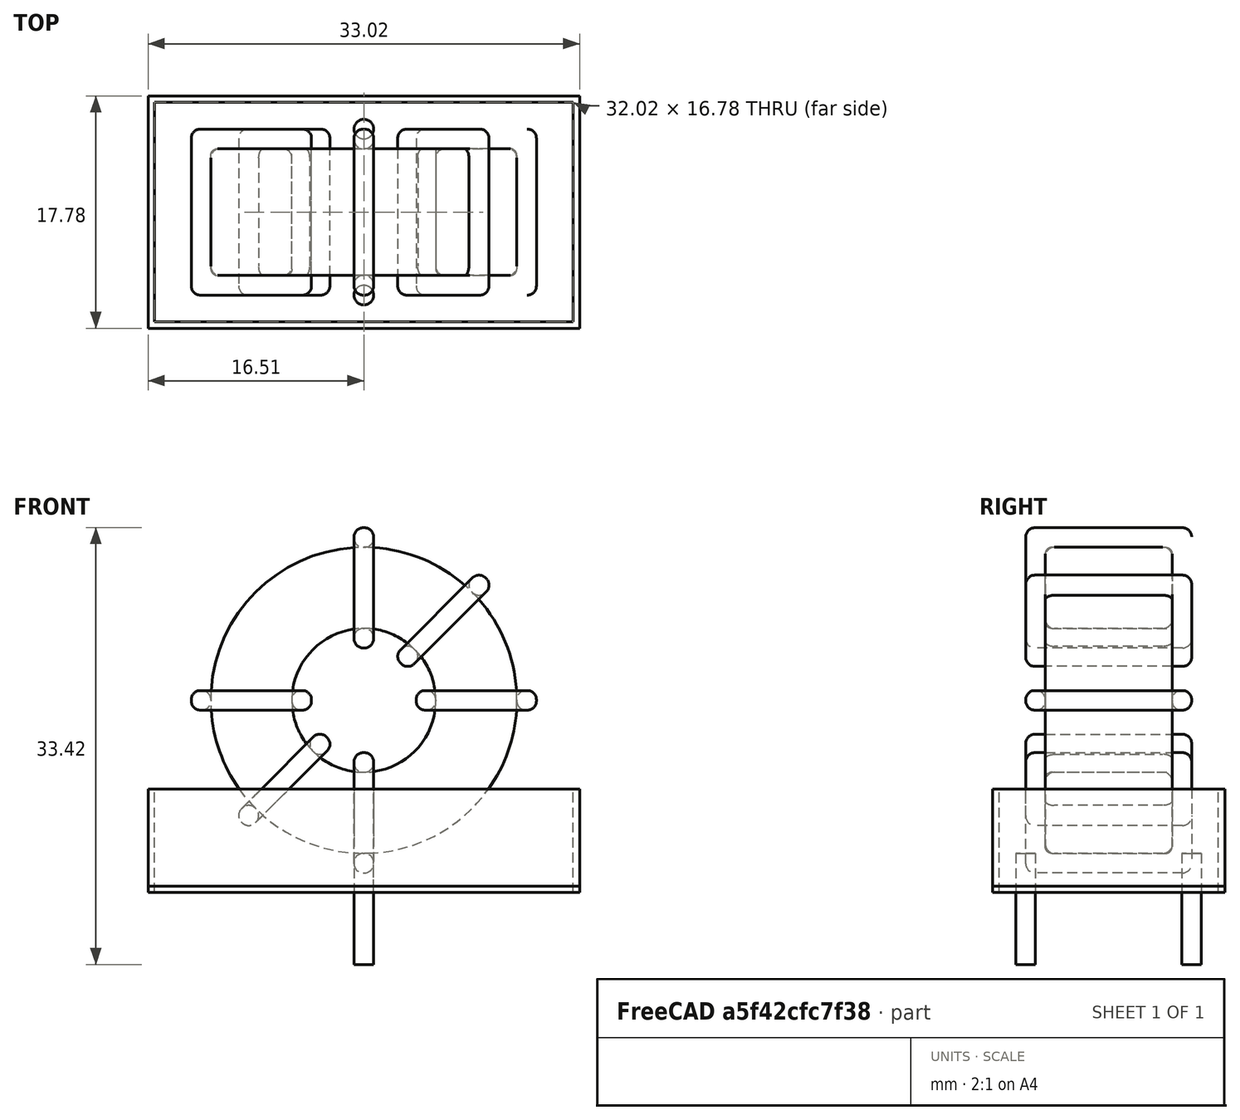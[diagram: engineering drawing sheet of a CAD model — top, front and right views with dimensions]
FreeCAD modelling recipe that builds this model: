
FCSTD DOCUMENT  (FreeCAD 0.16R6703 (Git))
Label: L_Toroid_Vertical_L33.0mm_W17.8mm_P12.70mm_Pulse_KM-5
License: All rights reserved
LicenseURL: http://en.wikipedia.org/wiki/All_rights_reserved
objects: Sketcher::SketchObject×8, PartDesign::Pad×8, PartDesign::Fillet×5, Spreadsheet::Sheet×1
note: 29 computed .brp shape members not serialized (recipe doc carries the construction recipe); baked Part::Feature solids carry a one-line shape summary decoded from their .brp

FEATURE [Spreadsheet::Sheet] Spreadsheet  label="dimensions"
  cells = A1=Wx; B1(Wx)=26.416; C1(WW)=11.00666666666667; D1(iWx)=33.02; A2=Wy; B2(Wy)=12.7; D2(iWy)=17.78; A3=RM; B3(RMx)=12.7; C3(RMy)=0; A4=d_wire; B4(d_wire)=1.5; A5=H; B5(H)=33.02; A6=offsetx; B6(offsetx)=16.51
FEATURE [Sketcher::SketchObject] Sketch
  Placement = pos=(0,-6.35,0) rot=(1,0,0;1.5708rad)
  expr: Placement.Base.y = -Spreadsheet.RMx / 2
  expr: Constraints[0] = Spreadsheet.Wx / 2 - Spreadsheet.d_wire
  expr: Constraints[4] = Spreadsheet.WW / 2
  expr: Constraints[2] = Spreadsheet.Wx / 2 + Spreadsheet.d_wire + 0.5
  sketch-geometry (2):
    g0: Circle CenterX=0 CenterY=15.208 CenterZ=0 NormalX=0 NormalY=0 NormalZ=1 Radius=11.708
    g1: Circle CenterX=0 CenterY=15.208 CenterZ=0 NormalX=0 NormalY=0 NormalZ=1 Radius=5.50333
  constraints (5):
    c: Radius(g0) = 11.708
    c: DistanceX(g-1,g0) = 0
    c: DistanceY(g-1,g0) = 15.208
    c: Coincident(g1,g0)
    c: Radius(g1) = 5.50333
FEATURE [PartDesign::Pad] Pad
  Length = 9.7
  Length2 = 100
  Midplane = true
  Placement = pos=(0,-6.35,0) rot=(1,0,0;1.5708rad)
  Sketch = -> Sketch
  Type = 0
  expr: Length = Spreadsheet.Wy - 2 * Spreadsheet.d_wire
FEATURE [Sketcher::SketchObject] Sketch001
  Placement = pos=(0,0,2) rot=(0,0,1;0rad)
  expr: Placement.Base.z = 0.5 + Spreadsheet.d_wire
  expr: Constraints[4] = Spreadsheet.RMy
  expr: Constraints[2] = -Spreadsheet.RMx
  expr: Constraints[1] = Spreadsheet.d_wire / 2
  sketch-geometry (2):
    g0: Circle CenterX=0 CenterY=0 CenterZ=0 NormalX=0 NormalY=0 NormalZ=1 Radius=0.75
    g1: Circle CenterX=0 CenterY=-12.7 CenterZ=0 NormalX=0 NormalY=0 NormalZ=1 Radius=0.75
  constraints (5):
    c: Equal(g0,g1)
    c: Radius(g0) = 0.75
    c: DistanceY(g-1,g1) = -12.7
    c: Coincident(g0,g-1)
    c: DistanceX(g-1,g1) = 0
FEATURE [PartDesign::Pad] Pad001
  Length = 1.5
  Length2 = 7
  Placement = pos=(0,0,2) rot=(0,0,1;0rad)
  Reversed = true
  Sketch = -> Sketch001
  Type = 4
  expr: Length2 = 5.5 + Spreadsheet.d_wire
  expr: Length = Spreadsheet.d_wire
FEATURE [PartDesign::Fillet] Fillet
  Base = -> Pad [Edge6,Edge3,Edge2]
  Placement = pos=(0,-6.35,0) rot=(1,0,0;1.5708rad)
  Radius = 0.5
FEATURE [Sketcher::SketchObject] Sketch003
  Placement = pos=(0,0,15.208) rot=(1,0,0;3.14159rad)
  expr: Constraints[18] = Spreadsheet.d_wire
  expr: Constraints[16] = Spreadsheet.d_wire
  expr: Constraints[19] = Spreadsheet.d_wire
  expr: Constraints[17] = Spreadsheet.d_wire
  expr: Placement.Base.y = -1 * (Spreadsheet.RMx - Spreadsheet.Wy) / 2
  expr: Constraints[21] = (Spreadsheet.Wx - Spreadsheet.WW) / 2 - Spreadsheet.d_wire
  expr: Constraints[22] = Spreadsheet.Wx / 2 - Spreadsheet.d_wire
  expr: Constraints[43] = Spreadsheet.d_wire
  expr: Constraints[48] = Spreadsheet.Wx - Spreadsheet.d_wire * 2
  expr: Constraints[49] = Spreadsheet.Wy
  expr: Placement.Base.z = Spreadsheet.Wx / 2 + Spreadsheet.d_wire + 0.5
  sketch-geometry (16):
    g0: LineSegment StartX=-4.00333 StartY=0 StartZ=0 EndX=-13.208 EndY=0 EndZ=0
    g1: LineSegment StartX=-13.208 StartY=0 StartZ=0 EndX=-13.208 EndY=12.7 EndZ=0
    g2: LineSegment StartX=-13.208 StartY=12.7 StartZ=0 EndX=-4.00333 EndY=12.7 EndZ=0
    g3: LineSegment StartX=-4.00333 StartY=12.7 StartZ=0 EndX=-4.00333 EndY=0 EndZ=0
    g4: LineSegment StartX=-11.708 StartY=11.2 StartZ=0 EndX=-5.50333 EndY=11.2 EndZ=0
    g5: LineSegment StartX=-5.50333 StartY=11.2 StartZ=0 EndX=-5.50333 EndY=1.5 EndZ=0
    g6: LineSegment StartX=-5.50333 StartY=1.5 StartZ=0 EndX=-11.708 EndY=1.5 EndZ=0
    g7: LineSegment StartX=-11.708 StartY=1.5 StartZ=0 EndX=-11.708 EndY=11.2 EndZ=0
    g8: LineSegment StartX=4.00333 StartY=12.7 StartZ=0 EndX=13.208 EndY=12.7 EndZ=0
    g9: LineSegment StartX=13.208 StartY=12.7 StartZ=0 EndX=13.208 EndY=0 EndZ=0
    g10: LineSegment StartX=13.208 StartY=0 StartZ=0 EndX=4.00333 EndY=0 EndZ=0
    g11: LineSegment StartX=4.00333 StartY=0 StartZ=0 EndX=4.00333 EndY=12.7 EndZ=0
    g12: LineSegment StartX=5.50333 StartY=11.2 StartZ=0 EndX=11.708 EndY=11.2 EndZ=0
    g13: LineSegment StartX=11.708 StartY=11.2 StartZ=0 EndX=11.708 EndY=1.5 EndZ=0
    g14: LineSegment StartX=11.708 StartY=1.5 StartZ=0 EndX=5.50333 EndY=1.5 EndZ=0
    g15: LineSegment StartX=5.50333 StartY=1.5 StartZ=0 EndX=5.50333 EndY=11.2 EndZ=0
  constraints (50):
    c: Horizontal(g0)
    c: Coincident(g1,g0)
    c: Vertical(g1)
    c: Coincident(g2,g1)
    c: Horizontal(g2)
    c: Coincident(g3,g2)
    c: Coincident(g3,g0)
    c: Vertical(g3)
    c: Coincident(g4,g5)
    c: Coincident(g5,g6)
    c: Coincident(g6,g7)
    c: Coincident(g7,g4)
    c: Horizontal(g4)
    c: Horizontal(g6)
    c: Vertical(g5)
    c: Vertical(g7)
    c: DistanceX(g1,g4) = 1.5
    c: DistanceY(g4,g1) = 1.5
    c: DistanceX(g5,g0) = 1.5
    c: DistanceY(g0,g5) = 1.5
    c: DistanceY(g-1,g0) = 0
    c: DistanceX(g6,g6) = 6.20467
    c: DistanceX(g6,g-1) = 11.708
    c: Coincident(g8,g9)
    c: Coincident(g9,g10)
    c: Coincident(g10,g11)
    c: Coincident(g11,g8)
    c: Horizontal(g8)
    c: Horizontal(g10)
    c: Vertical(g9)
    c: Vertical(g11)
    c: Coincident(g12,g13)
    c: Coincident(g13,g14)
    c: Coincident(g14,g15)
    c: Coincident(g15,g12)
    c: Horizontal(g12)
    c: Horizontal(g14)
    c: Vertical(g13)
    c: Vertical(g15)
    c: DistanceY(g8,g2) = 0
    c: DistanceY(g10,g0) = 0
    c: DistanceY(g14,g5) = 0
    c: DistanceY(g12,g4) = 0
    c: DistanceX(g8,g12) = 1.5
    c: Equal(g8,g2)
    c: Equal(g12,g4)
    c: Equal(g9,g1)
    c: Equal(g13,g7)
    c: DistanceX(g4,g12) = 23.416
    c: DistanceY(g0,g1) = 12.7
FEATURE [PartDesign::Pad] Pad002
  Length = 1.5
  Length2 = 100
  Midplane = true
  Placement = pos=(0,0,15.208) rot=(1,0,0;3.14159rad)
  Sketch = -> Sketch003
  Type = 0
  expr: Length = Spreadsheet.d_wire
FEATURE [PartDesign::Fillet] Fillet001
  Base = -> Pad002 [Edge38,Edge41,Edge42,Edge43,Edge29,Edge32,Edge33,Edge34,Edge25,Edge35,Edge36,Edge13,Edge14,Edge15,Edge16,Edge17,Edge18,Edge19,Edge1,Edge2,Edge3,Edge4,Edge5,Edge6,Edge7,Edge37,Edge39,Edge40,Edge20,Edge23,Edge24,Edge21,Edge22,Edge8,Edge9,Edge10,Edge11,Edge12,Edge26,Edge27,+8 more]
  Placement = pos=(0,0,15.208) rot=(1,0,0;3.14159rad)
  Radius = 0.705
  expr: Radius = Spreadsheet.d_wire * 0.47
FEATURE [Sketcher::SketchObject] Sketch004
  Placement = pos=(0,0,15.208) rot=(0.92388,0,0.382683;3.14159rad)
  expr: Constraints[18] = Spreadsheet.d_wire
  expr: Constraints[16] = Spreadsheet.d_wire
  expr: Constraints[19] = Spreadsheet.d_wire
  expr: Constraints[17] = Spreadsheet.d_wire
  expr: Placement.Base.y = -1 * (Spreadsheet.RMx - Spreadsheet.Wy) / 2
  expr: Constraints[21] = (Spreadsheet.Wx - Spreadsheet.WW) / 2 - Spreadsheet.d_wire
  expr: Constraints[22] = Spreadsheet.Wx / 2 - Spreadsheet.d_wire
  expr: Constraints[43] = Spreadsheet.d_wire
  expr: Constraints[48] = Spreadsheet.Wx - 2 * Spreadsheet.d_wire
  expr: Constraints[49] = Spreadsheet.Wy
  expr: Placement.Base.z = Spreadsheet.Wx / 2 + Spreadsheet.d_wire + 0.5
  sketch-geometry (16):
    g0: LineSegment StartX=-4.00333 StartY=0 StartZ=0 EndX=-13.208 EndY=0 EndZ=0
    g1: LineSegment StartX=-13.208 StartY=0 StartZ=0 EndX=-13.208 EndY=12.7 EndZ=0
    g2: LineSegment StartX=-13.208 StartY=12.7 StartZ=0 EndX=-4.00333 EndY=12.7 EndZ=0
    g3: LineSegment StartX=-4.00333 StartY=12.7 StartZ=0 EndX=-4.00333 EndY=0 EndZ=0
    g4: LineSegment StartX=-11.708 StartY=11.2 StartZ=0 EndX=-5.50333 EndY=11.2 EndZ=0
    g5: LineSegment StartX=-5.50333 StartY=11.2 StartZ=0 EndX=-5.50333 EndY=1.5 EndZ=0
    g6: LineSegment StartX=-5.50333 StartY=1.5 StartZ=0 EndX=-11.708 EndY=1.5 EndZ=0
    g7: LineSegment StartX=-11.708 StartY=1.5 StartZ=0 EndX=-11.708 EndY=11.2 EndZ=0
    g8: LineSegment StartX=4.00333 StartY=12.7 StartZ=0 EndX=13.208 EndY=12.7 EndZ=0
    g9: LineSegment StartX=13.208 StartY=12.7 StartZ=0 EndX=13.208 EndY=0 EndZ=0
    g10: LineSegment StartX=13.208 StartY=0 StartZ=0 EndX=4.00333 EndY=0 EndZ=0
    g11: LineSegment StartX=4.00333 StartY=0 StartZ=0 EndX=4.00333 EndY=12.7 EndZ=0
    g12: LineSegment StartX=5.50333 StartY=11.2 StartZ=0 EndX=11.708 EndY=11.2 EndZ=0
    g13: LineSegment StartX=11.708 StartY=11.2 StartZ=0 EndX=11.708 EndY=1.5 EndZ=0
    g14: LineSegment StartX=11.708 StartY=1.5 StartZ=0 EndX=5.50333 EndY=1.5 EndZ=0
    g15: LineSegment StartX=5.50333 StartY=1.5 StartZ=0 EndX=5.50333 EndY=11.2 EndZ=0
  constraints (50):
    c: Horizontal(g0)
    c: Coincident(g1,g0)
    c: Vertical(g1)
    c: Coincident(g2,g1)
    c: Horizontal(g2)
    c: Coincident(g3,g2)
    c: Coincident(g3,g0)
    c: Vertical(g3)
    c: Coincident(g4,g5)
    c: Coincident(g5,g6)
    c: Coincident(g6,g7)
    c: Coincident(g7,g4)
    c: Horizontal(g4)
    c: Horizontal(g6)
    c: Vertical(g5)
    c: Vertical(g7)
    c: DistanceX(g1,g4) = 1.5
    c: DistanceY(g4,g1) = 1.5
    c: DistanceX(g5,g0) = 1.5
    c: DistanceY(g0,g5) = 1.5
    c: DistanceY(g-1,g0) = 0
    c: DistanceX(g6,g6) = 6.20467
    c: DistanceX(g6,g-1) = 11.708
    c: Coincident(g8,g9)
    c: Coincident(g9,g10)
    c: Coincident(g10,g11)
    c: Coincident(g11,g8)
    c: Horizontal(g8)
    c: Horizontal(g10)
    c: Vertical(g9)
    c: Vertical(g11)
    c: Coincident(g12,g13)
    c: Coincident(g13,g14)
    c: Coincident(g14,g15)
    c: Coincident(g15,g12)
    c: Horizontal(g12)
    c: Horizontal(g14)
    c: Vertical(g13)
    c: Vertical(g15)
    c: DistanceY(g8,g2) = 0
    c: DistanceY(g10,g0) = 0
    c: DistanceY(g14,g5) = 0
    c: DistanceY(g12,g4) = 0
    c: DistanceX(g8,g12) = 1.5
    c: Equal(g8,g2)
    c: Equal(g12,g4)
    c: Equal(g9,g1)
    c: Equal(g13,g7)
    c: DistanceX(g4,g12) = 23.416
    c: DistanceY(g0,g1) = 12.7
FEATURE [PartDesign::Pad] Pad003
  Length = 1.5
  Length2 = 100
  Midplane = true
  Placement = pos=(0,0,15.208) rot=(0.92388,0,0.382683;3.14159rad)
  Sketch = -> Sketch004
  Type = 0
  expr: Length = Spreadsheet.d_wire
FEATURE [PartDesign::Fillet] Fillet002
  Base = -> Pad003 [Edge38,Edge41,Edge42,Edge43,Edge29,Edge32,Edge33,Edge34,Edge25,Edge35,Edge36,Edge13,Edge14,Edge15,Edge16,Edge17,Edge18,Edge19,Edge1,Edge2,Edge3,Edge4,Edge5,Edge6,Edge7,Edge37,Edge39,Edge40,Edge20,Edge23,Edge24,Edge21,Edge22,Edge8,Edge9,Edge10,Edge11,Edge12,Edge26,Edge27,+8 more]
  Placement = pos=(0,0,15.208) rot=(0.92388,0,0.382683;3.14159rad)
  Radius = 0.705
  expr: Radius = Spreadsheet.d_wire * 0.47
FEATURE [Sketcher::SketchObject] Sketch005
  Placement = pos=(0,0,15.208) rot=(0.92388,0,-0.382683;3.14159rad)
  expr: Constraints[18] = Spreadsheet.d_wire
  expr: Constraints[16] = Spreadsheet.d_wire
  expr: Constraints[19] = Spreadsheet.d_wire
  expr: Constraints[17] = Spreadsheet.d_wire
  expr: Placement.Base.y = -1 * (Spreadsheet.RMx - Spreadsheet.Wy) / 2
  expr: Constraints[21] = (Spreadsheet.Wx - Spreadsheet.WW) / 2 - Spreadsheet.d_wire
  expr: Constraints[22] = Spreadsheet.Wx / 2 - Spreadsheet.d_wire
  expr: Constraints[43] = Spreadsheet.d_wire
  expr: Constraints[48] = Spreadsheet.Wx - 2 * Spreadsheet.d_wire
  expr: Constraints[49] = Spreadsheet.Wy
  expr: Placement.Base.z = Spreadsheet.Wx / 2 + Spreadsheet.d_wire + 0.5
  sketch-geometry (16):
    g0: LineSegment StartX=-4.00333 StartY=0 StartZ=0 EndX=-13.208 EndY=0 EndZ=0
    g1: LineSegment StartX=-13.208 StartY=0 StartZ=0 EndX=-13.208 EndY=12.7 EndZ=0
    g2: LineSegment StartX=-13.208 StartY=12.7 StartZ=0 EndX=-4.00333 EndY=12.7 EndZ=0
    g3: LineSegment StartX=-4.00333 StartY=12.7 StartZ=0 EndX=-4.00333 EndY=0 EndZ=0
    g4: LineSegment StartX=-11.708 StartY=11.2 StartZ=0 EndX=-5.50333 EndY=11.2 EndZ=0
    g5: LineSegment StartX=-5.50333 StartY=11.2 StartZ=0 EndX=-5.50333 EndY=1.5 EndZ=0
    g6: LineSegment StartX=-5.50333 StartY=1.5 StartZ=0 EndX=-11.708 EndY=1.5 EndZ=0
    g7: LineSegment StartX=-11.708 StartY=1.5 StartZ=0 EndX=-11.708 EndY=11.2 EndZ=0
    g8: LineSegment StartX=4.00333 StartY=12.7 StartZ=0 EndX=13.208 EndY=12.7 EndZ=0
    g9: LineSegment StartX=13.208 StartY=12.7 StartZ=0 EndX=13.208 EndY=0 EndZ=0
    g10: LineSegment StartX=13.208 StartY=0 StartZ=0 EndX=4.00333 EndY=0 EndZ=0
    g11: LineSegment StartX=4.00333 StartY=0 StartZ=0 EndX=4.00333 EndY=12.7 EndZ=0
    g12: LineSegment StartX=5.50333 StartY=11.2 StartZ=0 EndX=11.708 EndY=11.2 EndZ=0
    g13: LineSegment StartX=11.708 StartY=11.2 StartZ=0 EndX=11.708 EndY=1.5 EndZ=0
    g14: LineSegment StartX=11.708 StartY=1.5 StartZ=0 EndX=5.50333 EndY=1.5 EndZ=0
    g15: LineSegment StartX=5.50333 StartY=1.5 StartZ=0 EndX=5.50333 EndY=11.2 EndZ=0
  constraints (50):
    c: Horizontal(g0)
    c: Coincident(g1,g0)
    c: Vertical(g1)
    c: Coincident(g2,g1)
    c: Horizontal(g2)
    c: Coincident(g3,g2)
    c: Coincident(g3,g0)
    c: Vertical(g3)
    c: Coincident(g4,g5)
    c: Coincident(g5,g6)
    c: Coincident(g6,g7)
    c: Coincident(g7,g4)
    c: Horizontal(g4)
    c: Horizontal(g6)
    c: Vertical(g5)
    c: Vertical(g7)
    c: DistanceX(g1,g4) = 1.5
    c: DistanceY(g4,g1) = 1.5
    c: DistanceX(g5,g0) = 1.5
    c: DistanceY(g0,g5) = 1.5
    c: DistanceY(g-1,g0) = 0
    c: DistanceX(g6,g6) = 6.20467
    c: DistanceX(g6,g-1) = 11.708
    c: Coincident(g8,g9)
    c: Coincident(g9,g10)
    c: Coincident(g10,g11)
    c: Coincident(g11,g8)
    c: Horizontal(g8)
    c: Horizontal(g10)
    c: Vertical(g9)
    c: Vertical(g11)
    c: Coincident(g12,g13)
    c: Coincident(g13,g14)
    c: Coincident(g14,g15)
    c: Coincident(g15,g12)
    c: Horizontal(g12)
    c: Horizontal(g14)
    c: Vertical(g13)
    c: Vertical(g15)
    c: DistanceY(g8,g2) = 0
    c: DistanceY(g10,g0) = 0
    c: DistanceY(g14,g5) = 0
    c: DistanceY(g12,g4) = 0
    c: DistanceX(g8,g12) = 1.5
    c: Equal(g8,g2)
    c: Equal(g12,g4)
    c: Equal(g9,g1)
    c: Equal(g13,g7)
    c: DistanceX(g4,g12) = 23.416
    c: DistanceY(g0,g1) = 12.7
FEATURE [PartDesign::Pad] Pad004
  Length = 1.5
  Length2 = 100
  Midplane = true
  Placement = pos=(0,0,15.208) rot=(0.92388,0,-0.382683;3.14159rad)
  Sketch = -> Sketch005
  Type = 0
  expr: Length = Spreadsheet.d_wire
FEATURE [PartDesign::Fillet] Fillet003
  Base = -> Pad004 [Edge38,Edge41,Edge42,Edge43,Edge29,Edge32,Edge33,Edge34,Edge25,Edge35,Edge36,Edge13,Edge14,Edge15,Edge16,Edge17,Edge18,Edge19,Edge1,Edge2,Edge3,Edge4,Edge5,Edge6,Edge7,Edge37,Edge39,Edge40,Edge20,Edge23,Edge24,Edge21,Edge22,Edge8,Edge9,Edge10,Edge11,Edge12,Edge26,Edge27,+8 more]
  Placement = pos=(0,0,15.208) rot=(0.92388,0,-0.382683;3.14159rad)
  Radius = 0.705
  expr: Radius = Spreadsheet.d_wire * 0.47
FEATURE [Sketcher::SketchObject] Sketch006
  Placement = pos=(0,0,15.208) rot=(0.707107,0,0.707107;3.14159rad)
  expr: Constraints[18] = Spreadsheet.d_wire
  expr: Constraints[16] = Spreadsheet.d_wire
  expr: Constraints[19] = Spreadsheet.d_wire
  expr: Constraints[17] = Spreadsheet.d_wire
  expr: Placement.Base.y = -1 * (Spreadsheet.RMx - Spreadsheet.Wy) / 2
  expr: Constraints[21] = (Spreadsheet.Wx - Spreadsheet.WW) / 2 - Spreadsheet.d_wire
  expr: Constraints[22] = Spreadsheet.Wx / 2 - Spreadsheet.d_wire
  expr: Constraints[43] = Spreadsheet.d_wire
  expr: Constraints[48] = Spreadsheet.Wx - Spreadsheet.d_wire * 2
  expr: Constraints[49] = Spreadsheet.Wy
  expr: Placement.Base.z = Spreadsheet.Wx / 2 + Spreadsheet.d_wire + 0.5
  sketch-geometry (16):
    g0: LineSegment StartX=-4.00333 StartY=0 StartZ=0 EndX=-13.208 EndY=0 EndZ=0
    g1: LineSegment StartX=-13.208 StartY=0 StartZ=0 EndX=-13.208 EndY=12.7 EndZ=0
    g2: LineSegment StartX=-13.208 StartY=12.7 StartZ=0 EndX=-4.00333 EndY=12.7 EndZ=0
    g3: LineSegment StartX=-4.00333 StartY=12.7 StartZ=0 EndX=-4.00333 EndY=0 EndZ=0
    g4: LineSegment StartX=-11.708 StartY=11.2 StartZ=0 EndX=-5.50333 EndY=11.2 EndZ=0
    g5: LineSegment StartX=-5.50333 StartY=11.2 StartZ=0 EndX=-5.50333 EndY=1.5 EndZ=0
    g6: LineSegment StartX=-5.50333 StartY=1.5 StartZ=0 EndX=-11.708 EndY=1.5 EndZ=0
    g7: LineSegment StartX=-11.708 StartY=1.5 StartZ=0 EndX=-11.708 EndY=11.2 EndZ=0
    g8: LineSegment StartX=4.00333 StartY=12.7 StartZ=0 EndX=13.208 EndY=12.7 EndZ=0
    g9: LineSegment StartX=13.208 StartY=12.7 StartZ=0 EndX=13.208 EndY=0 EndZ=0
    g10: LineSegment StartX=13.208 StartY=0 StartZ=0 EndX=4.00333 EndY=0 EndZ=0
    g11: LineSegment StartX=4.00333 StartY=0 StartZ=0 EndX=4.00333 EndY=12.7 EndZ=0
    g12: LineSegment StartX=5.50333 StartY=11.2 StartZ=0 EndX=11.708 EndY=11.2 EndZ=0
    g13: LineSegment StartX=11.708 StartY=11.2 StartZ=0 EndX=11.708 EndY=1.5 EndZ=0
    g14: LineSegment StartX=11.708 StartY=1.5 StartZ=0 EndX=5.50333 EndY=1.5 EndZ=0
    g15: LineSegment StartX=5.50333 StartY=1.5 StartZ=0 EndX=5.50333 EndY=11.2 EndZ=0
  constraints (50):
    c: Horizontal(g0)
    c: Coincident(g1,g0)
    c: Vertical(g1)
    c: Coincident(g2,g1)
    c: Horizontal(g2)
    c: Coincident(g3,g2)
    c: Coincident(g3,g0)
    c: Vertical(g3)
    c: Coincident(g4,g5)
    c: Coincident(g5,g6)
    c: Coincident(g6,g7)
    c: Coincident(g7,g4)
    c: Horizontal(g4)
    c: Horizontal(g6)
    c: Vertical(g5)
    c: Vertical(g7)
    c: DistanceX(g1,g4) = 1.5
    c: DistanceY(g4,g1) = 1.5
    c: DistanceX(g5,g0) = 1.5
    c: DistanceY(g0,g5) = 1.5
    c: DistanceY(g-1,g0) = 0
    c: DistanceX(g6,g6) = 6.20467
    c: DistanceX(g6,g-1) = 11.708
    c: Coincident(g8,g9)
    c: Coincident(g9,g10)
    c: Coincident(g10,g11)
    c: Coincident(g11,g8)
    c: Horizontal(g8)
    c: Horizontal(g10)
    c: Vertical(g9)
    c: Vertical(g11)
    c: Coincident(g12,g13)
    c: Coincident(g13,g14)
    c: Coincident(g14,g15)
    c: Coincident(g15,g12)
    c: Horizontal(g12)
    c: Horizontal(g14)
    c: Vertical(g13)
    c: Vertical(g15)
    c: DistanceY(g8,g2) = 0
    c: DistanceY(g10,g0) = 0
    c: DistanceY(g14,g5) = 0
    c: DistanceY(g12,g4) = 0
    c: DistanceX(g8,g12) = 1.5
    c: Equal(g8,g2)
    c: Equal(g12,g4)
    c: Equal(g9,g1)
    c: Equal(g13,g7)
    c: DistanceX(g4,g12) = 23.416
    c: DistanceY(g0,g1) = 12.7
FEATURE [PartDesign::Pad] Pad005
  Length = 1.5
  Length2 = 100
  Midplane = true
  Placement = pos=(0,0,15.208) rot=(0.707107,0,0.707107;3.14159rad)
  Sketch = -> Sketch006
  Type = 0
  expr: Length = Spreadsheet.d_wire
FEATURE [PartDesign::Fillet] Fillet004
  Base = -> Pad005 [Edge38,Edge41,Edge42,Edge43,Edge29,Edge32,Edge33,Edge34,Edge25,Edge35,Edge36,Edge13,Edge14,Edge15,Edge16,Edge17,Edge18,Edge19,Edge1,Edge2,Edge3,Edge4,Edge5,Edge6,Edge7,Edge37,Edge39,Edge40,Edge20,Edge23,Edge24,Edge21,Edge22,Edge8,Edge9,Edge10,Edge11,Edge12,Edge26,Edge27,+8 more]
  Placement = pos=(0,0,15.208) rot=(0.707107,0,0.707107;3.14159rad)
  Radius = 0.705
  expr: Radius = Spreadsheet.d_wire * 0.47
FEATURE [Sketcher::SketchObject] Sketch007
  Placement = pos=(0,0,0.5) rot=(0,0,1;0rad)
  expr: Placement.Base.z = 0.5
  expr: Constraints[11] = Spreadsheet.iWx / 2
  expr: Constraints[10] = (Spreadsheet.iWy - Spreadsheet.RMx) / 2
  expr: Constraints[9] = Spreadsheet.iWy
  expr: Constraints[8] = Spreadsheet.iWx
  sketch-geometry (4):
    g0: LineSegment StartX=-16.51 StartY=2.54 StartZ=0 EndX=16.51 EndY=2.54 EndZ=0
    g1: LineSegment StartX=16.51 StartY=2.54 StartZ=0 EndX=16.51 EndY=-15.24 EndZ=0
    g2: LineSegment StartX=16.51 StartY=-15.24 StartZ=0 EndX=-16.51 EndY=-15.24 EndZ=0
    g3: LineSegment StartX=-16.51 StartY=-15.24 StartZ=0 EndX=-16.51 EndY=2.54 EndZ=0
  constraints (12):
    c: Coincident(g0,g1)
    c: Coincident(g1,g2)
    c: Coincident(g2,g3)
    c: Coincident(g3,g0)
    c: Horizontal(g0)
    c: Horizontal(g2)
    c: Vertical(g1)
    c: Vertical(g3)
    c: DistanceX(g0,g0) = 33.02
    c: DistanceY(g3,g3) = 17.78
    c: DistanceY(g-1,g0) = 2.54
    c: DistanceX(g0,g-1) = 16.51
FEATURE [PartDesign::Pad] Pad006
  Length = 0.5
  Length2 = 100
  Placement = pos=(0,0,0.5) rot=(0,0,1;0rad)
  Sketch = -> Sketch007
  Type = 0
FEATURE [Sketcher::SketchObject] Sketch008
  Placement = pos=(0,0,0.5) rot=(0,0,1;0rad)
  expr: Constraints[8] = Spreadsheet.iWx
  expr: Constraints[9] = Spreadsheet.iWy
  expr: Constraints[10] = (Spreadsheet.iWy - Spreadsheet.RMx) / 2
  expr: Placement.Base.z = 0.5
  expr: Constraints[21] = 0.5
  expr: Constraints[11] = Spreadsheet.iWx / 2
  sketch-geometry (8):
    g0: LineSegment StartX=-16.51 StartY=2.54 StartZ=0 EndX=16.51 EndY=2.54 EndZ=0
    g1: LineSegment StartX=16.51 StartY=2.54 StartZ=0 EndX=16.51 EndY=-15.24 EndZ=0
    g2: LineSegment StartX=16.51 StartY=-15.24 StartZ=0 EndX=-16.51 EndY=-15.24 EndZ=0
    g3: LineSegment StartX=-16.51 StartY=-15.24 StartZ=0 EndX=-16.51 EndY=2.54 EndZ=0
    g4: LineSegment StartX=-16.01 StartY=2.04 StartZ=0 EndX=16.01 EndY=2.04 EndZ=0
    g5: LineSegment StartX=16.01 StartY=2.04 StartZ=0 EndX=16.01 EndY=-14.74 EndZ=0
    g6: LineSegment StartX=16.01 StartY=-14.74 StartZ=0 EndX=-16.01 EndY=-14.74 EndZ=0
    g7: LineSegment StartX=-16.01 StartY=-14.74 StartZ=0 EndX=-16.01 EndY=2.04 EndZ=0
  constraints (24):
    c: Coincident(g0,g1)
    c: Coincident(g1,g2)
    c: Coincident(g2,g3)
    c: Coincident(g3,g0)
    c: Horizontal(g0)
    c: Horizontal(g2)
    c: Vertical(g1)
    c: Vertical(g3)
    c: DistanceX(g0,g0) = 33.02
    c: DistanceY(g3,g3) = 17.78
    c: DistanceY(g-1,g0) = 2.54
    c: DistanceX(g0,g-1) = 16.51
    c: Coincident(g4,g5)
    c: Coincident(g5,g6)
    c: Coincident(g6,g7)
    c: Coincident(g7,g4)
    c: Horizontal(g4)
    c: Horizontal(g6)
    c: Vertical(g5)
    c: Vertical(g7)
    c: DistanceX(g5,g1) = 0.5
    c: DistanceY(g1,g5) = 0.5
    c: DistanceX(g0,g4) = 0.5
    c: DistanceY(g4,g0) = 0.5
FEATURE [PartDesign::Pad] Pad007
  Length = 7.9248
  Length2 = 100
  Placement = pos=(0,0,0.5) rot=(0,0,1;0rad)
  Sketch = -> Sketch008
  Type = 0
  expr: Length = Spreadsheet.Wx * 0.3
